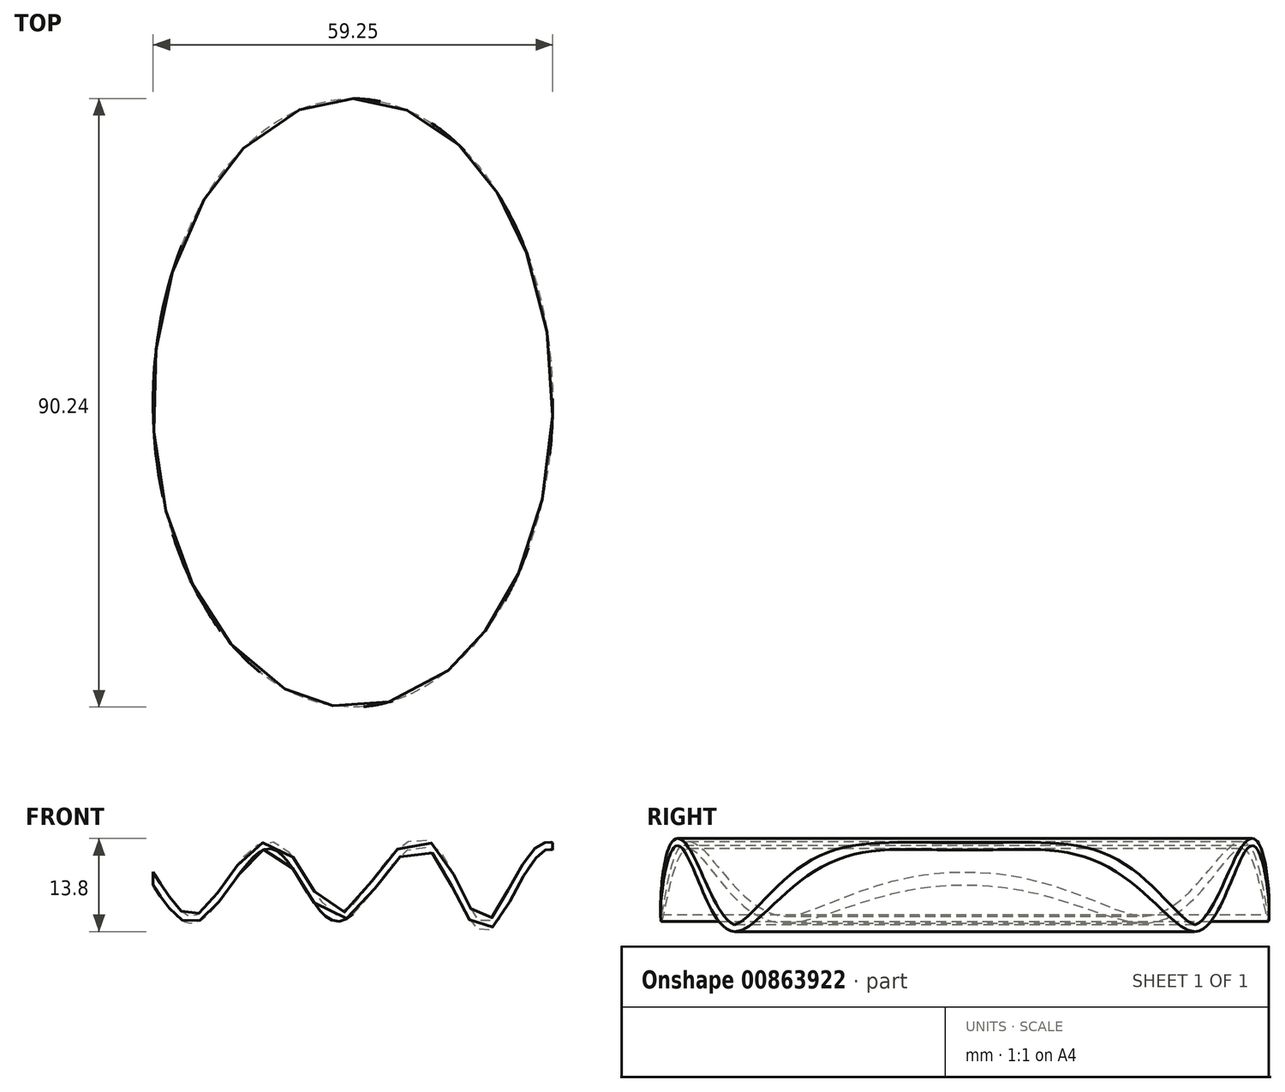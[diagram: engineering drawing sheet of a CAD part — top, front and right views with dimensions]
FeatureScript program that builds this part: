
annotation { "Feature Type Name" : "Feature", "Feature Type Description" : "" }
export const myFeature = defineFeature(function(context is Context, id is Id, definition is map)
    precondition{}
    {
        {
            var Q0;
            Q0=qCreatedBy(makeId("Front.planeOp"),FACE);
            var sketch = newSketch(context, id + "F0", { "sketchPlane" : qUnion([Q0])});
            skFitSpline(sketch, "E0", {"points": [v(0, 0) * mm, v(8.03, 6.6) * mm, v(18.65, -5.08) * mm, v(30.12, 5.96) * mm, v(40.1, -4.87) * mm, v(52.43, 6.39) * mm, v(61.78, -6.36) * mm, v(71.28, 5.82) * mm, v(80.94, -7.06) * mm, v(91.36, 5.05) * mm], "startDerivative": vector(86.4, 131.64) * mm, "endDerivative": vector(93.44, 186.3) * mm});
            skFitSpline(sketch, "E1.0", {"points": [v(-0.85, 0.56) * mm, v(-0.4, 1.24) * mm, v(0.5, 2.62) * mm, v(1.9, 4.57) * mm, v(3.1, 5.96) * mm, v(4.1, 6.86) * mm, v(4.92, 7.42) * mm, v(5.8, 7.8) * mm, v(6.77, 7.98) * mm, v(7.6, 7.87) * mm, v(8.25, 7.64) * mm, v(8.87, 7.3) * mm, v(9.57, 6.75) * mm, v(10.35, 5.93) * mm, v(11.1, 4.99) * mm, v(12.08, 3.6) * mm, v(13.29, 1.68) * mm, v(14.49, -0.21) * mm, v(15.44, -1.57) * mm, v(16.14, -2.46) * mm, v(16.82, -3.2) * mm, v(17.46, -3.72) * mm, v(17.93, -3.97) * mm, v(18.24, -4.06) * mm, v(18.44, -4.08) * mm, v(18.64, -4.07) * mm, v(18.87, -4.01) * mm, v(19.13, -3.9) * mm, v(19.53, -3.67) * mm, v(20.1, -3.23) * mm, v(20.83, -2.49) * mm, v(21.6, -1.57) * mm, v(22.64, -0.2) * mm, v(23.7, 1.32) * mm, v(24.78, 2.82) * mm, v(25.6, 3.9) * mm, v(26.42, 4.88) * mm, v(27.27, 5.74) * mm, v(28.01, 6.32) * mm, v(28.66, 6.68) * mm, v(29.18, 6.88) * mm, v(29.74, 7) * mm, v(30.33, 6.99) * mm, v(30.89, 6.86) * mm, v(31.4, 6.64) * mm, v(31.88, 6.35) * mm, v(32.46, 5.9) * mm, v(33.12, 5.2) * mm, v(33.87, 4.24) * mm, v(34.58, 3.17) * mm, v(35.28, 2.04) * mm, v(36.2, 0.5) * mm, v(37.11, -0.98) * mm, v(38, -2.23) * mm, v(38.66, -3) * mm, v(39.17, -3.45) * mm, v(39.53, -3.68) * mm, v(39.77, -3.79) * mm, v(39.98, -3.85) * mm, v(40.15, -3.86) * mm, v(40.35, -3.84) * mm, v(40.6, -3.77) * mm, v(40.88, -3.63) * mm, v(41.3, -3.37) * mm, v(41.9, -2.89) * mm, v(42.69, -2.09) * mm, v(43.77, -0.8) * mm, v(44.9, 0.7) * mm, v(46.04, 2.26) * mm, v(46.9, 3.4) * mm, v(47.78, 4.49) * mm, v(48.66, 5.47) * mm, v(49.56, 6.32) * mm, v(50.34, 6.88) * mm, v(51.03, 7.2) * mm, v(51.58, 7.37) * mm, v(52.16, 7.44) * mm, v(52.76, 7.38) * mm, v(53.32, 7.2) * mm, v(53.83, 6.93) * mm, v(54.3, 6.59) * mm, v(54.86, 6.06) * mm, v(55.5, 5.28) * mm, v(56.22, 4.2) * mm, v(56.9, 3) * mm, v(57.55, 1.73) * mm, v(58.18, 0.43) * mm, v(58.8, -0.85) * mm, v(59.4, -2.07) * mm, v(59.99, -3.18) * mm, v(60.56, -4.12) * mm, v(61, -4.72) * mm, v(61.32, -5.05) * mm, v(61.53, -5.22) * mm, v(61.69, -5.31) * mm, v(61.76, -5.34) * mm, v(61.8, -5.34) * mm, v(61.81, -5.34) * mm, v(61.87, -5.34) * mm, v(62, -5.28) * mm, v(62.25, -5.12) * mm, v(62.68, -4.72) * mm, v(63.27, -3.96) * mm, v(63.9, -3) * mm, v(64.54, -1.9) * mm, v(65.2, -0.68) * mm, v(65.87, 0.57) * mm, v(66.55, 1.82) * mm, v(67.23, 3.03) * mm, v(67.94, 4.16) * mm, v(68.66, 5.15) * mm, v(69.3, 5.85) * mm, v(69.87, 6.3) * mm, v(70.34, 6.59) * mm, v(70.86, 6.8) * mm, v(71.44, 6.87) * mm, v(72.01, 6.81) * mm, v(72.53, 6.64) * mm, v(73, 6.38) * mm, v(73.57, 5.96) * mm, v(74.21, 5.3) * mm, v(74.92, 4.37) * mm, v(75.6, 3.3) * mm, v(76.28, 2.13) * mm, v(77.16, 0.48) * mm, v(78.03, -1.2) * mm, v(78.89, -2.8) * mm, v(79.53, -3.89) * mm, v(80.16, -4.83) * mm, v(80.76, -5.6) * mm, v(81.31, -6.11) * mm, v(81.74, -6.35) * mm, v(82.09, -6.42) * mm, v(82.46, -6.38) * mm, v(82.93, -6.2) * mm, v(83.5, -5.8) * mm, v(84.11, -5.23) * mm, v(84.99, -4.23) * mm, v(86.14, -2.58) * mm, v(87.56, -0.14) * mm, v(89, 2.6) * mm, v(89.97, 4.54) * mm, v(90.46, 5.5) * mm]});
            skLineSegment(sketch, "E2", {"start": v(-0.85, 0.56) * mm, "end": v(0, 0) * mm});
            skLineSegment(sketch, "E3", {"start": v(91.36, 5.05) * mm, "end": v(90.46, 5.5) * mm});
            skSolve(sketch);
        }
        {
            var Q0;
            Q0 = qSketchRegion(id + "F0", true);
            extrude(context, id + "F1", {"entities" : qUnion([Q0]), "depth" : 101.6 * mm, "offsetDistance" : 25.4 * mm});
        }
        {
            var Q0;
            Q0=qCreatedBy(makeId("Top.planeOp"),FACE);
            var sketch = newSketch(context, id + "F2", { "sketchPlane" : qUnion([Q0])});
            skEllipse(sketch, "E4", {"center": v(42.41, -54.36) * mm, "majorRadius": 45.12 * mm, "minorRadius": 29.63 * mm, "majorAxis": v(0, 1)});
            skLineSegment(sketch, "E5.bottom", {"start": v(136.05, 52.79) * mm, "end": v(-43.88, 52.79) * mm});
            skLineSegment(sketch, "E5.top", {"start": v(136.05, -155) * mm, "end": v(-43.88, -155) * mm});
            skLineSegment(sketch, "E5.left", {"start": v(136.05, 52.79) * mm, "end": v(136.05, -155) * mm});
            skLineSegment(sketch, "E5.right", {"start": v(-43.88, 52.79) * mm, "end": v(-43.88, -155) * mm});
            skSolve(sketch);
        }
        {
            var Q0;
            Q0=makeQuery(id+"F2.imprint","IMPRINT",FACE,{"disambiguationData":[TD([[makeQuery(id+"F2.imprint","IMPRINT",EDGE,{"derivedFrom":sQuery(id+"F2.wireOp",EDGE,"E4")}),-1.0]])]});
            extrude(context, id + "F3", {"entities" : qUnion([Q0]), "operationType" : NewBodyOperationType.REMOVE, "depth" : 50.8 * mm, "offsetDistance" : 25.4 * mm, "hasSecondDirection" : true, "secondDirectionOppositeDirection" : true, "secondDirectionDepth" : 25.4 * mm});
        }
    });
